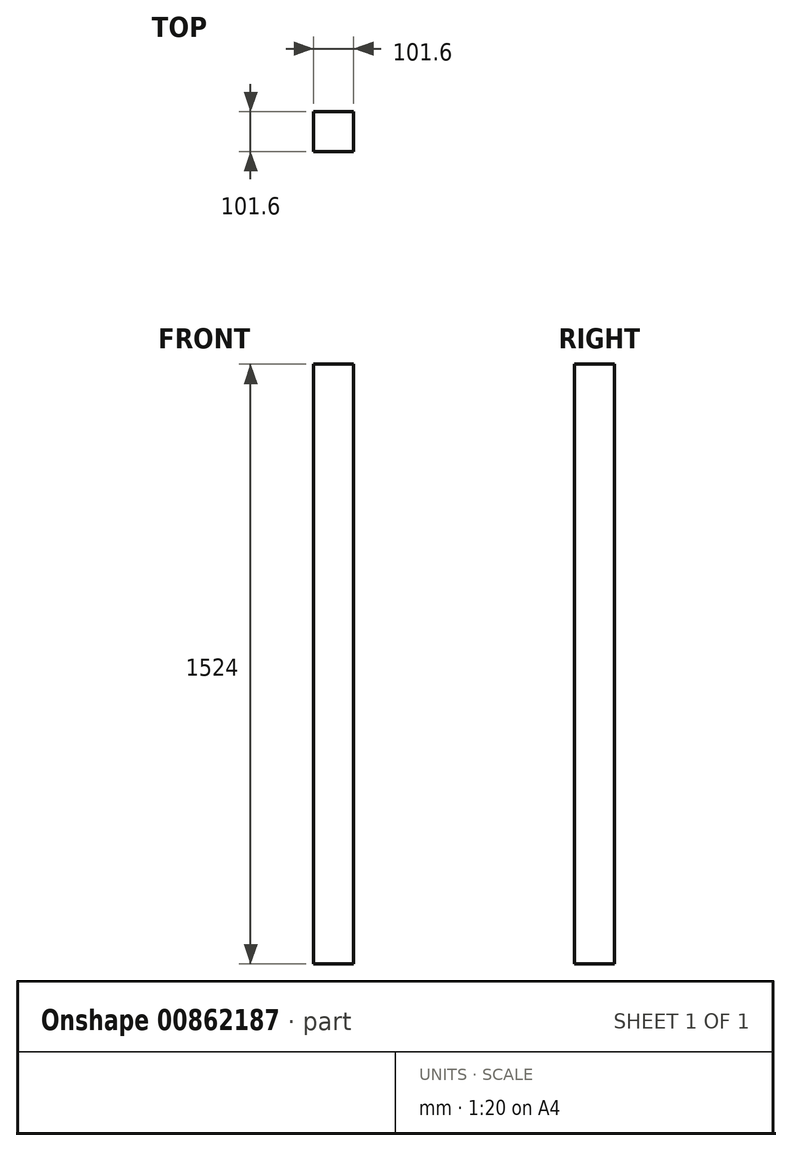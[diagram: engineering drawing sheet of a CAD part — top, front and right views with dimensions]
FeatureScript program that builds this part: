
annotation { "Feature Type Name" : "Feature", "Feature Type Description" : "" }
export const myFeature = defineFeature(function(context is Context, id is Id, definition is map)
    precondition{}
    {
        {
            var Q0;
            Q0=qCreatedBy(makeId("Top.planeOp"),FACE);
            var sketch = newSketch(context, id + "F0", { "sketchPlane" : qUnion([Q0])});
            skLineSegment(sketch, "E0.bottom", {"start": v(0, 0) * mm, "end": v(101.6, 0) * mm});
            skLineSegment(sketch, "E0.top", {"start": v(0, -101.6) * mm, "end": v(101.6, -101.6) * mm});
            skLineSegment(sketch, "E0.left", {"start": v(0, 0) * mm, "end": v(0, -101.6) * mm});
            skLineSegment(sketch, "E0.right", {"start": v(101.6, 0) * mm, "end": v(101.6, -101.6) * mm});
            skSolve(sketch);
        }
        {
            var Q0;
            Q0=makeQuery(id+"F0.imprint","IMPRINT",FACE,{"disambiguationData":[TD([[makeQuery(id+"F0.imprint","IMPRINT",EDGE,{"derivedFrom":sQuery(id+"F0.wireOp",EDGE,"E0.bottom")}),-1.0]])]});
            extrude(context, id + "F1", {"entities" : qUnion([Q0]), "depth" : 1524 * mm, "offsetDistance" : 25.4 * mm});
        }
    });
